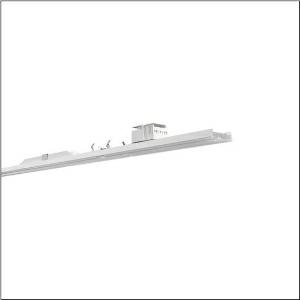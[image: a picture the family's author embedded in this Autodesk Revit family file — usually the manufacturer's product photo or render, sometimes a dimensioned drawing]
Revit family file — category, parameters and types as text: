
# Revit family: licross_r__11_recessed_mo_51tl18dn485fd_f4d7
name_source: partatom
category: Lighting Fixtures
units: mm (PartAtom-declared; Revit-internal decimal feet)

## family parameters
Cut with Voids When Loaded = No
Host = Face
Light Source = No
Part Type = Normal
Room Calculation Point = No
Round Connector Dimension = Use Diameter
Shared = No

## types (1)
- --- (1 x LED, 1420 lm, 9.8 W, 4000K)
    Apparent Load = 10 VA
    CIE Flux Codes = 83 96 99 100 100
    Color Rendering = 80
    Color Temperature = 4000K
    Default Elevation = 1800 mm
    Description = Licross® 11 Recessed MOluminaire insert, length: 1.500mm, width: 66mm, height: 67mm, LED rated luminous flux: 8.910lm, light colour: 840, control gear: DALI 2, control gear: ECG DALI, with plug, 6-pole, with phase selection, mains connection: 220..240V, AC/DC, 0/50..60Hz, without changeover relay, for emergency light function, for central battery installations according to DIN EN 60598-2-22, halogen-free wiring, primary optical cover: cover, of PMMA, light emission: direct distribution, protection rating (complete): IP40, insulation class (complete): insulation class I (protective earthing), certification: CE, ENEC, VDE, protection symbol: D if used in an environment without relevant dust loads with corresponding accessories, permissible ambient temperature for indoor applications: -25..+40°C, standard: EN 60598-2-22, reducing of maximum allowable ambient temperature of 5°C with ceiling mounting, corresponds to IFS (International Featured Standards) requirements for safety and quality in the food industry, packaging unit: 1 piece
    Height = 58 mm
    Lamp = 1 x LED
    Lamp Light Flux = 1420 lm
    Lamp Power = 9.8 W
    Lamp count = 1
    Length = 1500 mm
    Luminous efficacy = 145 lm/W
    Manufacturer = Siteco
    ModVariant = No
    Model = 51TL18DN485FD
    Mounting Place = Ceiling
    Mounting Type = Pendant
    Number of Poles = 1
    OnlyDefault = Yes
    Power Factor = 1
    Product Name = Licross® 11 Recessed MO
    Product group = luminaire insert
    ProductGroupID = 902
    Protection Class = Protection class I
    Protection Degree = IP 40
    RLX_Detail_Level = 1
    RlxData = <blob elided: 22609 chars, md5=e399442b>
    Socket = socket
    Standby Power = 0 W
    System Light Flux = 1420 lm
    System Power = 10 W
    Type Comments = : DC mode (central or group accumulator) initial emergency light level
    Type Image = l_1266722.jpg
    URL = http://relux.com
    VarID = @adj_134169
    Voltage = 0 V
    Weight = 0.00 kg
    Width = 66 mm

## geometry (parser evidence)
native form markers: Blend x4, Sweep x10
no freeform markers — native parametric forms only
